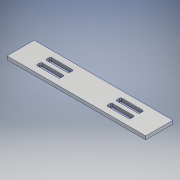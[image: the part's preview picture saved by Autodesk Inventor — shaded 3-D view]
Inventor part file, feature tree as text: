
AUTODESK INVENTOR PART (.ipt)
format: ipt  version: 2017 (Build 210142000, 142)  size: 143,872 bytes
history: native  units: mm
features: extrude x1, sketch x1
ambient origin geometry x8: Origin, YZ Plane, XZ Plane, XY Plane, X Axis, Y Axis, Z Axis, Center Point
bodies: Body1 (feature_tree)
feature tree (2):
  extrude  "Extrusion4"  Depth=9.525mm TaperAngle=0.0deg
  sketch  "Sketch1"  dims[d0=388.62mm d1=76.2mm d27=9.525mm d28=0.0mm]
